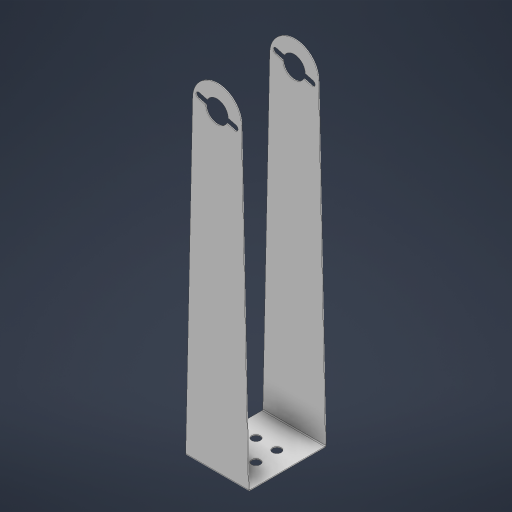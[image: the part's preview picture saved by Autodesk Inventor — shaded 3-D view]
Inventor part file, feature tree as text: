
AUTODESK INVENTOR PART (.ipt)
format: ipt  version: 2024 (Build 280153000, 153)  size: 264,192 bytes
history: native  units: mm
features: other x5, sketch x1
ambient origin geometry x8: Origin, YZ Plane, XZ Plane, XY Plane, X Axis, Y Axis, Z Axis, Center Point
bodies: Body1 (feature_tree)
feature tree (6):
  other  "Sólido1"
  sketch  "Boceto1"  dims[d3=18.0mm d7=5.0mm d8=6.0mm d9=6.0mm d10=40.0mm d12=360.0deg d14=14.0mm d15=180.0mm d16=0.5mm d17=0.5mm d18=0.25mm d19=1.0mm d20=0.5mm d21=90.0deg d22=0.5mm d23=0.5mm d24=0.25mm d25=1.0mm d26=0.5mm d27=90.0deg d28=0.5mm]
  other  "Cara1"
  other  "Pliegue1"
  other  "Pliegue2"
  other  "Placa1"
